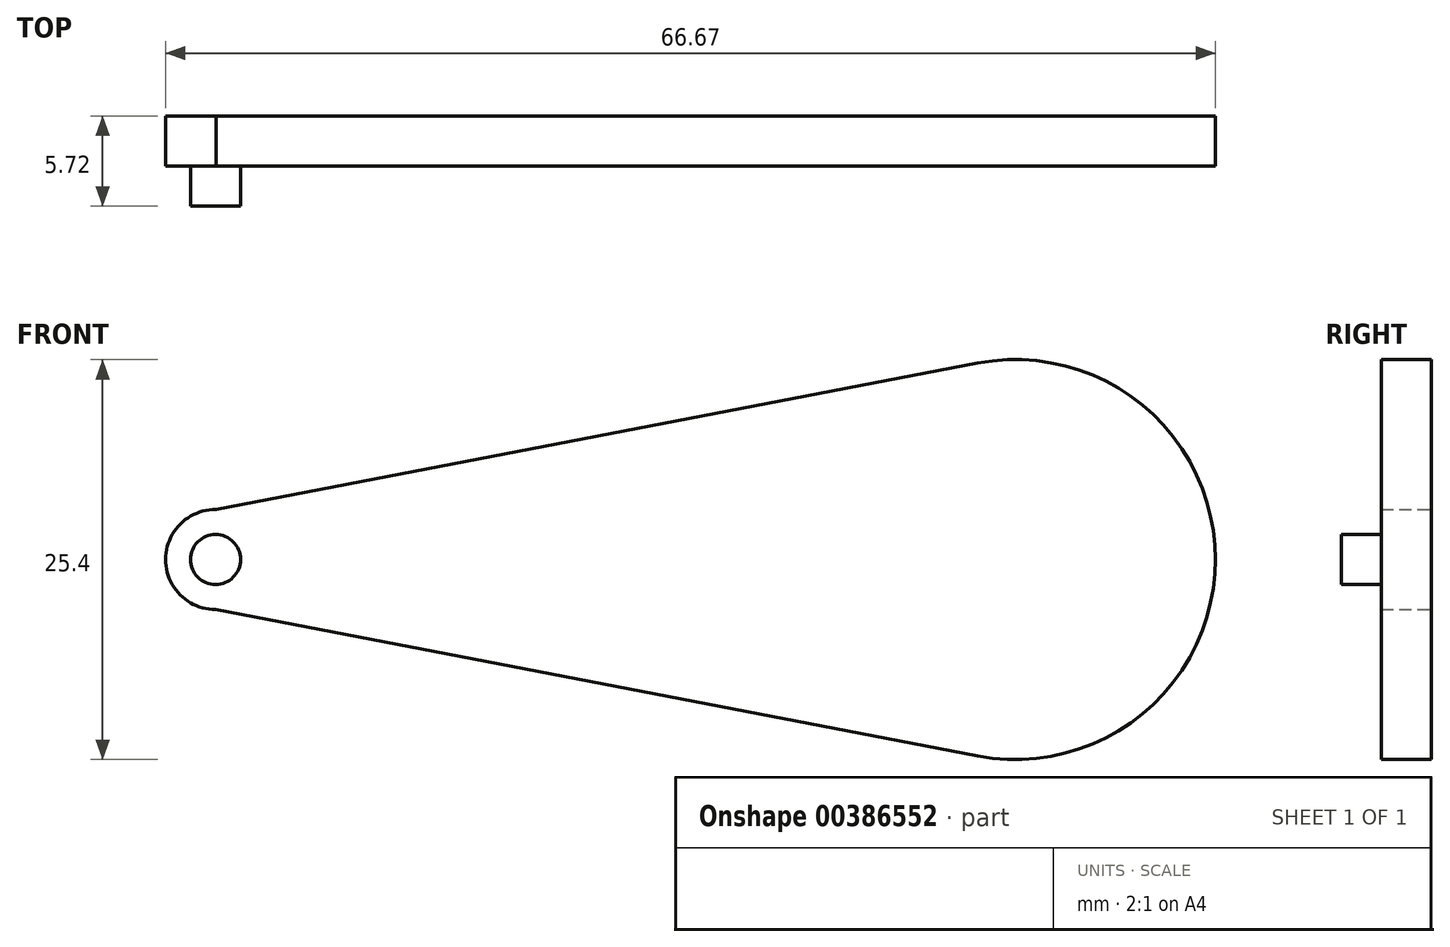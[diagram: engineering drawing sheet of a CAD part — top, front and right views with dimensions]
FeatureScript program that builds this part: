
annotation { "Feature Type Name" : "Feature", "Feature Type Description" : "" }
export const myFeature = defineFeature(function(context is Context, id is Id, definition is map)
    precondition{}
    {
        {
            var Q0;
            Q0=qCreatedBy(makeId("Front.planeOp"),FACE);
            var sketch = newSketch(context, id + "F0", { "sketchPlane" : qUnion([Q0])});
            skArc(sketch, "E0", {"start": v(-2.4, -12.47) * mm, "mid": v(12.7, 0) * mm, "end": v(-2.4, 12.47) * mm});
            skArc(sketch, "E1", {"start": v(-50.78, 3.17) * mm, "mid": v(-53.97, 0) * mm, "end": v(-50.8, -3.18) * mm});
            skLineSegment(sketch, "E2", {"start": v(-50.78, 3.17) * mm, "end": v(-2.4, 12.47) * mm});
            skLineSegment(sketch, "E3", {"start": v(-50.8, -3.17) * mm, "end": v(-2.4, -12.47) * mm});
            skSolve(sketch);
        }
        {
            var Q0;
            Q0=makeQuery(id+"F0.imprint","IMPRINT",FACE,{"disambiguationData":[TD([[makeQuery(id+"F0.imprint","IMPRINT",EDGE,{"derivedFrom":sQuery(id+"F0.wireOp",EDGE,"E0")}),1.0]])]});
            extrude(context, id + "F1", {"entities" : qUnion([Q0]), "depth" : 3.17 * mm});
        }
        {
            var Q0;
            Q0=makeQuery(id+"F1.opExtrude","CAP_FACE",FACE,{"disambiguationData":[OSD([sQuery(id+"F0.wireOp",EDGE,"E0"),sQuery(id+"F0.wireOp",EDGE,"E1"),sQuery(id+"F0.wireOp",EDGE,"E2"),sQuery(id+"F0.wireOp",EDGE,"E3")])],"isStart":false});
            var sketch = newSketch(context, id + "F2", { "sketchPlane" : qUnion([Q0])});
            skCircle(sketch, "E4", {"center": v(-50.8, 0) * mm, "radius": 1.59 * mm});
            skSolve(sketch);
        }
        {
            var Q0;
            Q0 = qSketchRegion(id + "F2", true);
            extrude(context, id + "F3", {"entities" : qUnion([Q0]), "operationType" : NewBodyOperationType.ADD, "depth" : 2.54 * mm});
        }
    });
